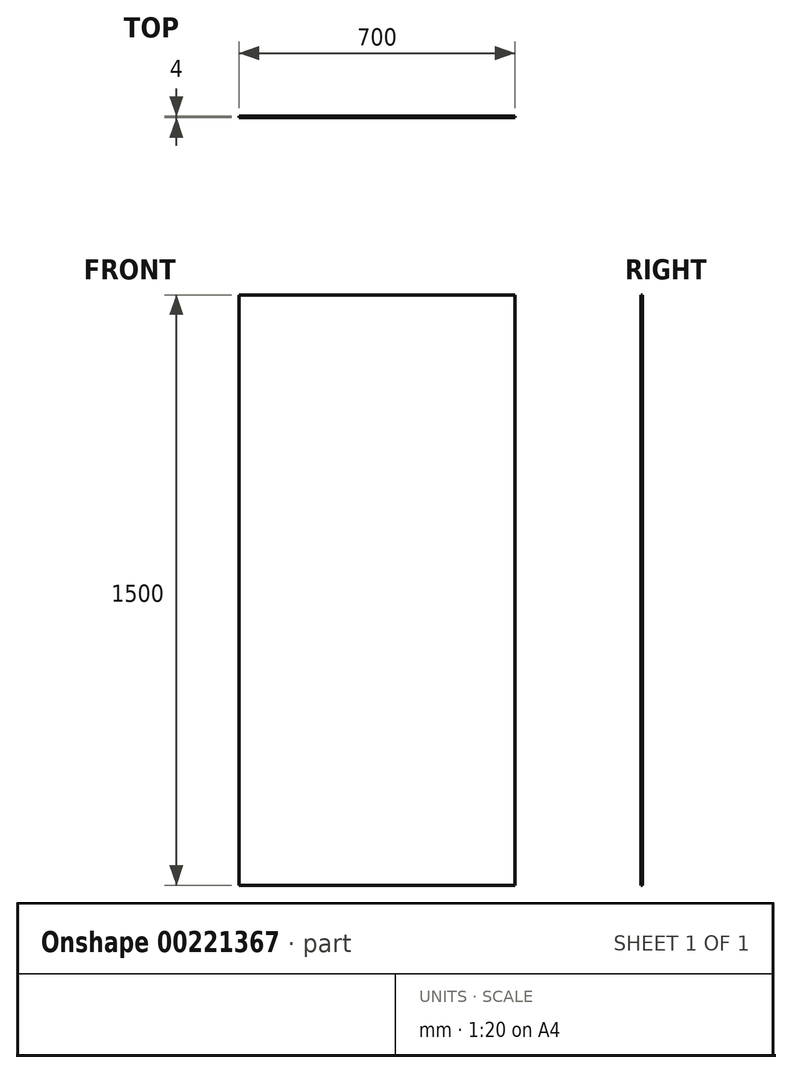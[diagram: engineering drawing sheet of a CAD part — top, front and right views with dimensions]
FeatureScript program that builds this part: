
annotation { "Feature Type Name" : "Feature", "Feature Type Description" : "" }
export const myFeature = defineFeature(function(context is Context, id is Id, definition is map)
    precondition{}
    {
        {
            var Q0;
            Q0=qCreatedBy(makeId("Front.planeOp"),FACE);
            var sketch = newSketch(context, id + "F0", { "sketchPlane" : qUnion([Q0])});
            skLineSegment(sketch, "E0.bottom", {"start": v(350, -750) * mm, "end": v(-350, -750) * mm});
            skLineSegment(sketch, "E0.top", {"start": v(350, 750) * mm, "end": v(-350, 750) * mm});
            skLineSegment(sketch, "E0.left", {"start": v(350, -750) * mm, "end": v(350, 750) * mm});
            skLineSegment(sketch, "E0.right", {"start": v(-350, -750) * mm, "end": v(-350, 750) * mm});
            skPoint(sketch, "E0.middle", {"position": v(0, 0) * mm});
            skSolve(sketch);
        }
        {
            var Q0;
            Q0 = qSketchRegion(id + "F0", true);
            extrude(context, id + "F1", {"entities" : qUnion([Q0]), "depth" : 4 * mm});
        }
    });
